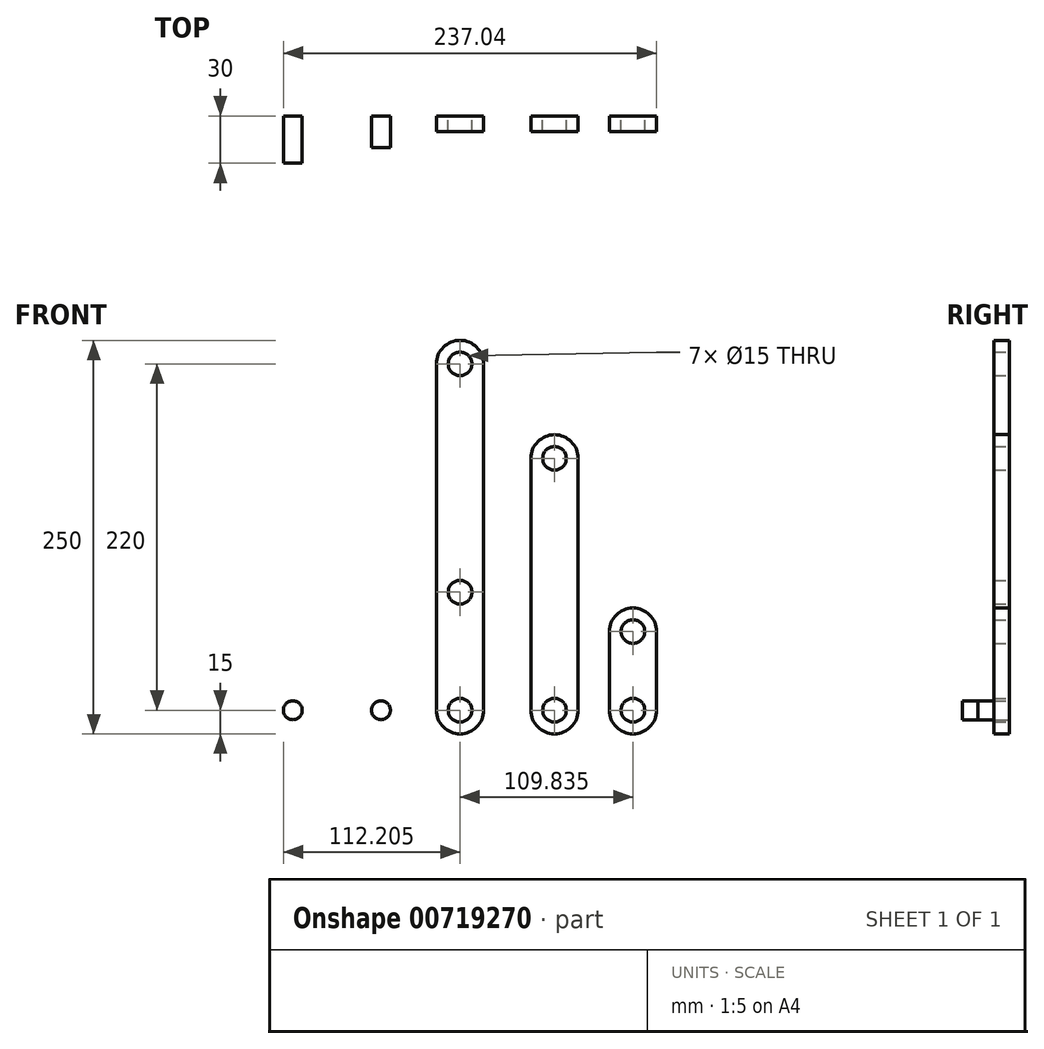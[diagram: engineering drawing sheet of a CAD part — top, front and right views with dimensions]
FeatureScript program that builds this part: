
annotation { "Feature Type Name" : "Feature", "Feature Type Description" : "" }
export const myFeature = defineFeature(function(context is Context, id is Id, definition is map)
    precondition{}
    {
        {
            assignVariable(context, id + "F0", {"name" : "thickness", "anyValue" : 10});
        }
        {
            var Q0;
            Q0=qCreatedBy(makeId("Front.planeOp"),FACE);
            var sketch = newSketch(context, id + "F1", { "sketchPlane" : qUnion([Q0])});
            skArc(sketch, "E0", {"start": v(-15, 0) * mm, "mid": v(0, -15) * mm, "end": v(15, 0) * mm});
            skCircle(sketch, "E1", {"center": v(0, 0) * mm, "radius": 7.5 * mm});
            skLineSegment(sketch, "E2", {"start": v(-15, 0) * mm, "end": v(-15, 50) * mm});
            skLineSegment(sketch, "E3", {"start": v(15, 0) * mm, "end": v(15, 50) * mm});
            skArc(sketch, "E4.MirrorC", {"start": v(-15, 50) * mm, "mid": v(0, 65) * mm, "end": v(15, 50) * mm});
            skCircle(sketch, "E5.MirrorC", {"center": v(0, 50) * mm, "radius": 7.5 * mm});
            skSolve(sketch);
        }
        {
            var Q0;
            Q0 = qSketchRegion(id + "F1", true);
            extrude(context, id + "F2", {"entities" : qUnion([Q0]), "depth" : (getVariable(context, 'thickness')) * mm, "offsetDistance" : 25 * mm});
        }
        {
            var Q0;
            Q0=qCreatedBy(makeId("Front.planeOp"),FACE);
            var sketch = newSketch(context, id + "F3", { "sketchPlane" : qUnion([Q0])});
            skCircle(sketch, "E6", {"center": v(-49.84, 0) * mm, "radius": 7.5 * mm});
            skArc(sketch, "E7", {"start": v(-64.84, 0) * mm, "mid": v(-49.84, -15) * mm, "end": v(-34.84, 0) * mm});
            skLineSegment(sketch, "E8", {"start": v(-64.84, 0) * mm, "end": v(-64.84, 160) * mm});
            skLineSegment(sketch, "E9", {"start": v(-34.84, 0) * mm, "end": v(-34.84, 160) * mm});
            skArc(sketch, "E10.MirrorC", {"start": v(-64.84, 160) * mm, "mid": v(-49.84, 175) * mm, "end": v(-34.84, 160) * mm});
            skCircle(sketch, "E11", {"center": v(-49.84, 160) * mm, "radius": 7.5 * mm});
            skSolve(sketch);
        }
        {
            var Q0;
            Q0=makeQuery(id+"F3.imprint","IMPRINT",FACE,{"disambiguationData":[TD([[makeQuery(id+"F3.imprint","IMPRINT",EDGE,{"derivedFrom":sQuery(id+"F3.wireOp",EDGE,"E6")}),-1.0]])]});
            extrude(context, id + "F4", {"entities" : qUnion([Q0]), "depth" : (getVariable(context, 'thickness')) * mm, "offsetDistance" : 25 * mm});
        }
        {
            var Q0;
            Q0=qCreatedBy(makeId("Front.planeOp"),FACE);
            var sketch = newSketch(context, id + "F5", { "sketchPlane" : qUnion([Q0])});
            skCircle(sketch, "E12", {"center": v(-109.84, 0) * mm, "radius": 7.5 * mm});
            skArc(sketch, "E13", {"start": v(-124.84, 0) * mm, "mid": v(-109.84, -15) * mm, "end": v(-94.84, 0) * mm});
            skLineSegment(sketch, "E14", {"start": v(-124.84, 0) * mm, "end": v(-124.84, 220) * mm});
            skLineSegment(sketch, "E15", {"start": v(-94.84, 0) * mm, "end": v(-94.84, 220) * mm});
            skArc(sketch, "E16.MirrorC", {"start": v(-124.84, 220) * mm, "mid": v(-109.84, 235) * mm, "end": v(-94.84, 220) * mm});
            skCircle(sketch, "E17", {"center": v(-109.84, 220) * mm, "radius": 7.5 * mm});
            skLineSegment(sketch, "E18", {"start": v(-109.84, 0) * mm, "end": v(-109.84, 75) * mm});
            skCircle(sketch, "E19", {"center": v(-109.84, 75) * mm, "radius": 7.5 * mm});
            skSolve(sketch);
        }
        {
            var Q0;
            Q0 = qSketchRegion(id + "F5", true);
            extrude(context, id + "F6", {"entities" : qUnion([Q0]), "depth" : (getVariable(context, 'thickness')) * mm, "offsetDistance" : 25 * mm});
        }
        {
            var Q0;
            Q0=qCreatedBy(makeId("Front.planeOp"),FACE);
            var sketch = newSketch(context, id + "F7", { "sketchPlane" : qUnion([Q0])});
            skCircle(sketch, "E20", {"center": v(-160.04, 0) * mm, "radius": 6 * mm});
            skSolve(sketch);
        }
        {
            var Q0;
            Q0=makeQuery(id+"F7.imprint","IMPRINT",FACE,{"disambiguationData":[TD([[makeQuery(id+"F7.imprint","IMPRINT",EDGE,{"derivedFrom":sQuery(id+"F7.wireOp",EDGE,"E20")}),1.0]])]});
            extrude(context, id + "F8", {"entities" : qUnion([Q0]), "depth" : 20 * mm, "offsetDistance" : 25 * mm});
        }
        {
            var Q0;
            Q0=qCreatedBy(makeId("Front.planeOp"),FACE);
            var sketch = newSketch(context, id + "F9", { "sketchPlane" : qUnion([Q0])});
            skCircle(sketch, "E21", {"center": v(-216.04, 0) * mm, "radius": 6 * mm});
            skSolve(sketch);
        }
        {
            var Q0;
            Q0 = qSketchRegion(id + "F9", true);
            extrude(context, id + "F10", {"entities" : qUnion([Q0]), "depth" : 30 * mm, "offsetDistance" : 25 * mm});
        }
    });
